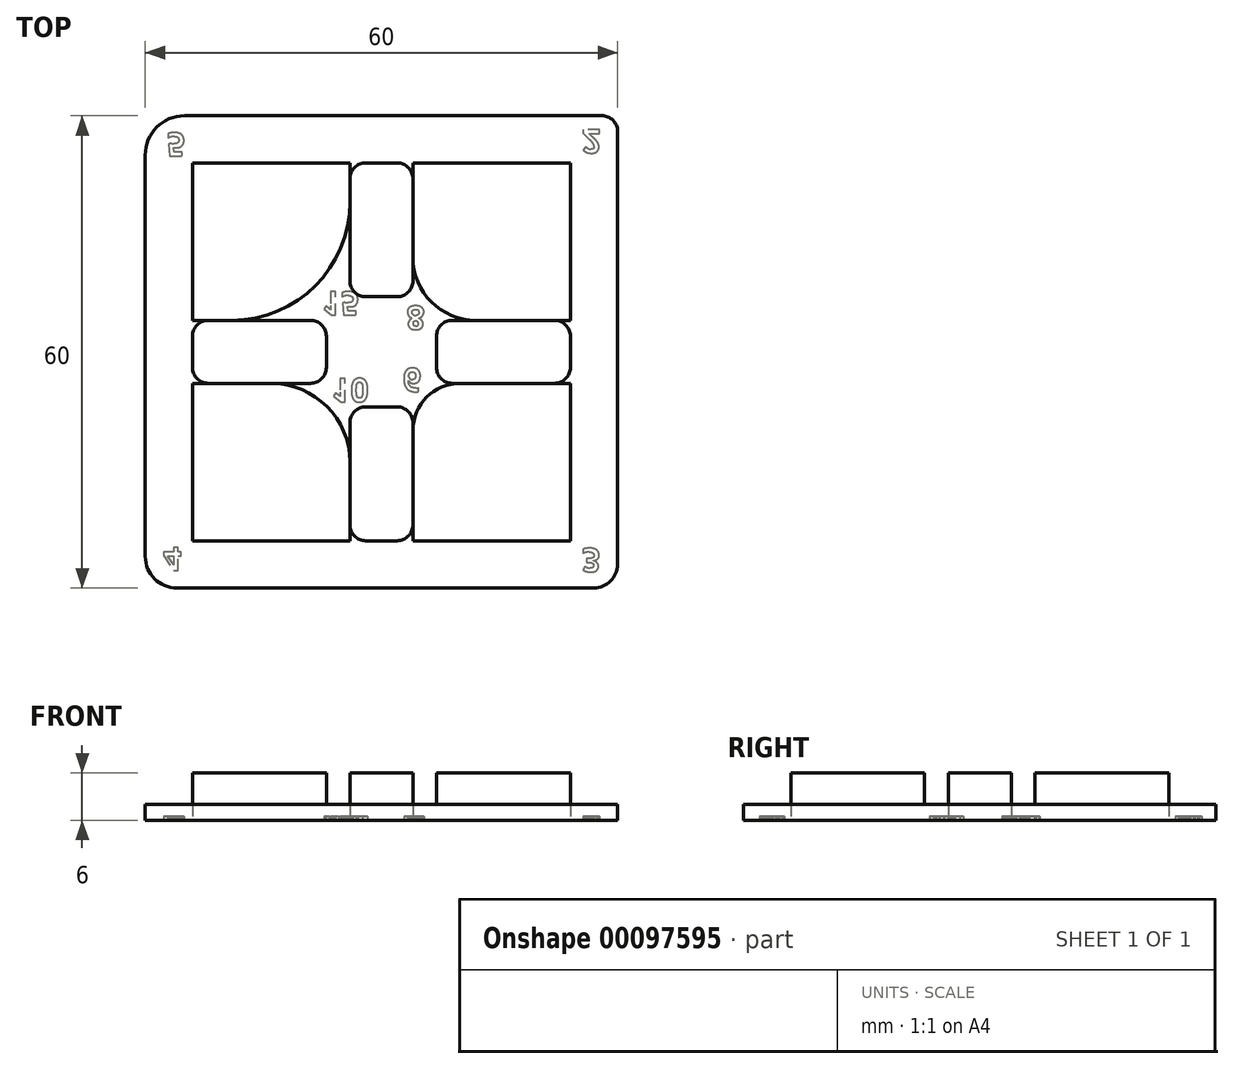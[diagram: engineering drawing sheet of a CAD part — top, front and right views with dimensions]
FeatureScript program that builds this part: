
annotation { "Feature Type Name" : "Feature", "Feature Type Description" : "" }
export const myFeature = defineFeature(function(context is Context, id is Id, definition is map)
    precondition{}
    {
        {
            var Q0;
            Q0=qCreatedBy(makeId("Top.planeOp"),FACE);
            var sketch = newSketch(context, id + "F0", { "sketchPlane" : qUnion([Q0])});
            skLineSegment(sketch, "E0.bottom", {"start": v(4, 0) * mm, "end": v(57, 0) * mm});
            skLineSegment(sketch, "E0.top", {"start": v(5, 60) * mm, "end": v(58, 60) * mm});
            skLineSegment(sketch, "E0.left", {"start": v(0, 4) * mm, "end": v(0, 55) * mm});
            skLineSegment(sketch, "E0.right", {"start": v(60, 3) * mm, "end": v(60, 58) * mm});
            skLineSegment(sketch, "E1.bottom", {"start": v(6, 6) * mm, "end": v(26, 6) * mm});
            skLineSegment(sketch, "E1.top", {"start": v(6, 26) * mm, "end": v(16, 26) * mm});
            skLineSegment(sketch, "E1.left", {"start": v(6, 6) * mm, "end": v(6, 26) * mm});
            skLineSegment(sketch, "E1.right", {"start": v(26, 6) * mm, "end": v(26, 16) * mm});
            skPoint(sketch, "E2.visualSharp", {"position": v(26, 26) * mm});
            skArc(sketch, "E2.filletArc", {"start": v(26, 16) * mm, "mid": v(23.07, 23.07) * mm, "end": v(16, 26) * mm});
            skLineSegment(sketch, "E3.bottom", {"start": v(6, 54) * mm, "end": v(26, 54) * mm});
            skLineSegment(sketch, "E3.top", {"start": v(6, 34) * mm, "end": v(11, 34) * mm});
            skLineSegment(sketch, "E3.left", {"start": v(6, 54) * mm, "end": v(6, 34) * mm});
            skLineSegment(sketch, "E3.right", {"start": v(26, 54) * mm, "end": v(26, 49) * mm});
            skPoint(sketch, "E4.visualSharp", {"position": v(26, 34) * mm});
            skArc(sketch, "E4.filletArc", {"start": v(11, 34) * mm, "mid": v(21.6, 38.4) * mm, "end": v(26, 49) * mm});
            skPoint(sketch, "E5.oppositeSnap0", {"position": v(8.5, 34) * mm});
            skLineSegment(sketch, "E5.bottom", {"start": v(54, 54) * mm, "end": v(34, 54) * mm});
            skLineSegment(sketch, "E5.top", {"start": v(54, 34) * mm, "end": v(42, 34) * mm});
            skLineSegment(sketch, "E5.left", {"start": v(54, 54) * mm, "end": v(54, 34) * mm});
            skLineSegment(sketch, "E5.right", {"start": v(34, 54) * mm, "end": v(34, 42) * mm});
            skPoint(sketch, "E6.visualSharp", {"position": v(34, 34) * mm});
            skArc(sketch, "E6.filletArc", {"start": v(34, 42) * mm, "mid": v(36.34, 36.34) * mm, "end": v(42, 34) * mm});
            skLineSegment(sketch, "E7.bottom", {"start": v(54, 6) * mm, "end": v(34, 6) * mm});
            skLineSegment(sketch, "E7.top", {"start": v(54, 26) * mm, "end": v(40, 26) * mm});
            skLineSegment(sketch, "E7.left", {"start": v(54, 6) * mm, "end": v(54, 26) * mm});
            skLineSegment(sketch, "E7.right", {"start": v(34, 6) * mm, "end": v(34, 20) * mm});
            skPoint(sketch, "E8.visualSharp", {"position": v(34, 26) * mm});
            skArc(sketch, "E8.filletArc", {"start": v(40, 26) * mm, "mid": v(35.76, 24.24) * mm, "end": v(34, 20) * mm});
            skPoint(sketch, "E9.visualSharp", {"position": v(0, 60) * mm});
            skArc(sketch, "E9.filletArc", {"start": v(5, 60) * mm, "mid": v(1.46, 58.54) * mm, "end": v(0, 55) * mm});
            skPoint(sketch, "E10.visualSharp", {"position": v(0, 0) * mm});
            skArc(sketch, "E10.filletArc", {"start": v(0, 4) * mm, "mid": v(1.17, 1.17) * mm, "end": v(4, 0) * mm});
            skPoint(sketch, "E11.visualSharp", {"position": v(60, 0) * mm});
            skArc(sketch, "E11.filletArc", {"start": v(57, 0) * mm, "mid": v(59.12, 0.88) * mm, "end": v(60, 3) * mm});
            skPoint(sketch, "E12.visualSharp", {"position": v(60, 60) * mm});
            skArc(sketch, "E12.filletArc", {"start": v(60, 58) * mm, "mid": v(59.41, 59.41) * mm, "end": v(58, 60) * mm});
            skSolve(sketch);
        }
        {
            var Q0;
            Q0=makeQuery(id+"F0.imprint","IMPRINT",FACE,{"disambiguationData":[TD([[makeQuery(id+"F0.imprint","IMPRINT",EDGE,{"derivedFrom":sQuery(id+"F0.wireOp",EDGE,"E0.bottom")}),1.0]])]});
            extrude(context, id + "F1", {"entities" : qUnion([Q0]), "depth" : 2 * mm, "offsetDistance" : 25 * mm});
        }
        {
            var Q0;
            Q0=makeQuery(id+"F1.opExtrude","CAP_FACE",FACE,{"disambiguationData":[OSD([sQuery(id+"F0.wireOp",EDGE,"E0.bottom"),sQuery(id+"F0.wireOp",EDGE,"E0.top"),sQuery(id+"F0.wireOp",EDGE,"E0.left"),sQuery(id+"F0.wireOp",EDGE,"E0.right"),sQuery(id+"F0.wireOp",EDGE,"E1.bottom"),sQuery(id+"F0.wireOp",EDGE,"E1.top"),sQuery(id+"F0.wireOp",EDGE,"E1.left"),sQuery(id+"F0.wireOp",EDGE,"E1.right"),sQuery(id+"F0.wireOp",EDGE,"E2.filletArc"),sQuery(id+"F0.wireOp",EDGE,"E3.bottom"),sQuery(id+"F0.wireOp",EDGE,"E3.top"),sQuery(id+"F0.wireOp",EDGE,"E3.left"),sQuery(id+"F0.wireOp",EDGE,"E3.right"),sQuery(id+"F0.wireOp",EDGE,"E4.filletArc"),sQuery(id+"F0.wireOp",EDGE,"E5.bottom"),sQuery(id+"F0.wireOp",EDGE,"E5.top"),sQuery(id+"F0.wireOp",EDGE,"E5.left"),sQuery(id+"F0.wireOp",EDGE,"E5.right"),sQuery(id+"F0.wireOp",EDGE,"E6.filletArc"),sQuery(id+"F0.wireOp",EDGE,"E7.bottom"),sQuery(id+"F0.wireOp",EDGE,"E7.top"),sQuery(id+"F0.wireOp",EDGE,"E7.left"),sQuery(id+"F0.wireOp",EDGE,"E7.right"),sQuery(id+"F0.wireOp",EDGE,"E8.filletArc")])],"isStart":false});
            var sketch = newSketch(context, id + "F2", { "sketchPlane" : qUnion([Q0])});
            skLineSegment(sketch, "E13.bottom", {"start": v(8, 26) * mm, "end": v(21, 26) * mm});
            skLineSegment(sketch, "E13.top", {"start": v(8, 34) * mm, "end": v(21, 34) * mm});
            skLineSegment(sketch, "E13.left", {"start": v(6, 28) * mm, "end": v(6, 32) * mm});
            skLineSegment(sketch, "E13.right", {"start": v(23, 28) * mm, "end": v(23, 32) * mm});
            skLineSegment(sketch, "E14.bottom", {"start": v(32, 54) * mm, "end": v(28, 54) * mm});
            skLineSegment(sketch, "E14.top", {"start": v(32, 37) * mm, "end": v(28, 37) * mm});
            skLineSegment(sketch, "E14.left", {"start": v(34, 52) * mm, "end": v(34, 39) * mm});
            skLineSegment(sketch, "E14.right", {"start": v(26, 52) * mm, "end": v(26, 39) * mm});
            skPoint(sketch, "E15.oppositeSnap0", {"position": v(36.34, 36.34) * mm});
            skLineSegment(sketch, "E16.bottom", {"start": v(32, 6) * mm, "end": v(28, 6) * mm});
            skLineSegment(sketch, "E16.top", {"start": v(32, 23) * mm, "end": v(28, 23) * mm});
            skLineSegment(sketch, "E16.left", {"start": v(34, 8) * mm, "end": v(34, 21) * mm});
            skLineSegment(sketch, "E16.right", {"start": v(26, 8) * mm, "end": v(26, 21) * mm});
            skLineSegment(sketch, "E17.bottom", {"start": v(52, 26) * mm, "end": v(39, 26) * mm});
            skLineSegment(sketch, "E17.top", {"start": v(52, 34) * mm, "end": v(39, 34) * mm});
            skLineSegment(sketch, "E17.left", {"start": v(54, 28) * mm, "end": v(54, 32) * mm});
            skLineSegment(sketch, "E17.right", {"start": v(37, 28) * mm, "end": v(37, 32) * mm});
            skPoint(sketch, "E18.visualSharp", {"position": v(6, 34) * mm});
            skArc(sketch, "E18.filletArc", {"start": v(8, 34) * mm, "mid": v(6.59, 33.41) * mm, "end": v(6, 32) * mm});
            skPoint(sketch, "E19.visualSharp", {"position": v(6, 26) * mm});
            skArc(sketch, "E19.filletArc", {"start": v(6, 28) * mm, "mid": v(6.59, 26.59) * mm, "end": v(8, 26) * mm});
            skPoint(sketch, "E20.visualSharp", {"position": v(23, 26) * mm});
            skArc(sketch, "E20.filletArc", {"start": v(21, 26) * mm, "mid": v(22.41, 26.59) * mm, "end": v(23, 28) * mm});
            skPoint(sketch, "E21.visualSharp", {"position": v(23, 34) * mm});
            skArc(sketch, "E21.filletArc", {"start": v(23, 32) * mm, "mid": v(22.41, 33.41) * mm, "end": v(21, 34) * mm});
            skPoint(sketch, "E22.visualSharp", {"position": v(26, 37) * mm});
            skArc(sketch, "E22.filletArc", {"start": v(26, 39) * mm, "mid": v(26.59, 37.59) * mm, "end": v(28, 37) * mm});
            skPoint(sketch, "E23.visualSharp", {"position": v(34, 37) * mm});
            skArc(sketch, "E23.filletArc", {"start": v(32, 37) * mm, "mid": v(33.41, 37.59) * mm, "end": v(34, 39) * mm});
            skPoint(sketch, "E24.visualSharp", {"position": v(34, 54) * mm});
            skArc(sketch, "E24.filletArc", {"start": v(34, 52) * mm, "mid": v(33.41, 53.41) * mm, "end": v(32, 54) * mm});
            skPoint(sketch, "E25.visualSharp", {"position": v(26, 54) * mm});
            skArc(sketch, "E25.filletArc", {"start": v(28, 54) * mm, "mid": v(26.59, 53.41) * mm, "end": v(26, 52) * mm});
            skPoint(sketch, "E26.visualSharp", {"position": v(37, 34) * mm});
            skArc(sketch, "E26.filletArc", {"start": v(39, 34) * mm, "mid": v(37.59, 33.41) * mm, "end": v(37, 32) * mm});
            skPoint(sketch, "E27.visualSharp", {"position": v(37, 26) * mm});
            skArc(sketch, "E27.filletArc", {"start": v(37, 28) * mm, "mid": v(37.59, 26.59) * mm, "end": v(39, 26) * mm});
            skPoint(sketch, "E28.visualSharp", {"position": v(54, 34) * mm});
            skArc(sketch, "E28.filletArc", {"start": v(54, 32) * mm, "mid": v(53.41, 33.41) * mm, "end": v(52, 34) * mm});
            skPoint(sketch, "E29.visualSharp", {"position": v(54, 26) * mm});
            skArc(sketch, "E29.filletArc", {"start": v(52, 26) * mm, "mid": v(53.41, 26.59) * mm, "end": v(54, 28) * mm});
            skPoint(sketch, "E30.visualSharp", {"position": v(26, 23) * mm});
            skArc(sketch, "E30.filletArc", {"start": v(28, 23) * mm, "mid": v(26.59, 22.41) * mm, "end": v(26, 21) * mm});
            skPoint(sketch, "E31.visualSharp", {"position": v(34, 23) * mm});
            skArc(sketch, "E31.filletArc", {"start": v(34, 21) * mm, "mid": v(33.41, 22.41) * mm, "end": v(32, 23) * mm});
            skPoint(sketch, "E32.visualSharp", {"position": v(34, 6) * mm});
            skArc(sketch, "E32.filletArc", {"start": v(32, 6) * mm, "mid": v(33.41, 6.59) * mm, "end": v(34, 8) * mm});
            skPoint(sketch, "E33.visualSharp", {"position": v(26, 6) * mm});
            skArc(sketch, "E33.filletArc", {"start": v(26, 8) * mm, "mid": v(26.59, 6.59) * mm, "end": v(28, 6) * mm});
            skSolve(sketch);
        }
        {
            var Q0;
            Q0 = qSketchRegion(id + "F2", true);
            extrude(context, id + "F3", {"entities" : qUnion([Q0]), "operationType" : NewBodyOperationType.ADD, "depth" : 4 * mm, "offsetDistance" : 25 * mm});
        }
        {
            var Q0;
            Q0=makeQuery(id+"F1.opExtrude","CAP_FACE",FACE,{"disambiguationData":[OSD([sQuery(id+"F0.wireOp",EDGE,"E0.bottom"),sQuery(id+"F0.wireOp",EDGE,"E0.top"),sQuery(id+"F0.wireOp",EDGE,"E0.left"),sQuery(id+"F0.wireOp",EDGE,"E0.right"),sQuery(id+"F0.wireOp",EDGE,"E1.bottom"),sQuery(id+"F0.wireOp",EDGE,"E1.top"),sQuery(id+"F0.wireOp",EDGE,"E1.left"),sQuery(id+"F0.wireOp",EDGE,"E1.right"),sQuery(id+"F0.wireOp",EDGE,"E2.filletArc"),sQuery(id+"F0.wireOp",EDGE,"E3.bottom"),sQuery(id+"F0.wireOp",EDGE,"E3.top"),sQuery(id+"F0.wireOp",EDGE,"E3.left"),sQuery(id+"F0.wireOp",EDGE,"E3.right"),sQuery(id+"F0.wireOp",EDGE,"E4.filletArc"),sQuery(id+"F0.wireOp",EDGE,"E5.bottom"),sQuery(id+"F0.wireOp",EDGE,"E5.top"),sQuery(id+"F0.wireOp",EDGE,"E5.left"),sQuery(id+"F0.wireOp",EDGE,"E5.right"),sQuery(id+"F0.wireOp",EDGE,"E6.filletArc"),sQuery(id+"F0.wireOp",EDGE,"E7.bottom"),sQuery(id+"F0.wireOp",EDGE,"E7.top"),sQuery(id+"F0.wireOp",EDGE,"E7.left"),sQuery(id+"F0.wireOp",EDGE,"E7.right"),sQuery(id+"F0.wireOp",EDGE,"E8.filletArc"),sQuery(id+"F0.wireOp",EDGE,"E9.filletArc"),sQuery(id+"F0.wireOp",EDGE,"E10.filletArc"),sQuery(id+"F0.wireOp",EDGE,"E11.filletArc"),sQuery(id+"F0.wireOp",EDGE,"E12.filletArc")])],"isStart":true});
            var sketch = newSketch(context, id + "F4", { "sketchPlane" : qUnion([Q0])});
            skText(sketch, "E34", { "text": "6\n", "fontName": "OpenSans-Bold.ttf"});
            skText(sketch, "E35", { "text": "10", "fontName": "OpenSans-Bold.ttf"});
            skText(sketch, "E36", { "text": "15", "fontName": "OpenSans-Bold.ttf"});
            skText(sketch, "E37", { "text": "8", "fontName": "OpenSans-Bold.ttf"});
            skText(sketch, "E38", { "text": "4", "fontName": "OpenSans-Bold.ttf"});
            skText(sketch, "E39", { "text": "5", "fontName": "OpenSans-Bold.ttf"});
            skText(sketch, "E40", { "text": "3", "fontName": "OpenSans-Bold.ttf"});
            skText(sketch, "E41", { "text": "2", "fontName": "OpenSans-Bold.ttf"});
            const initialGuessF4  = {"E34": [0.0327, -0.02792, 1, 0, 0.003], "E35": [0.02365, -0.02662, 1, 0, 0.003], "E36": [0.02244, -0.03763, 1, 0, 0.003], "E37": [0.03316, -0.03582, 1, 0, 0.003], "E38": [0.00223, -0.00517, 1, 0, 0.003], "E39": [0.00272, -0.05783, 1, 0, 0.003], "E40": [0.05543, -0.00503, 1, 0, 0.003], "E41": [0.05547, -0.05823, 1, 0, 0.003]};
            skSetInitialGuess(sketch, initialGuessF4);
            skSolve(sketch);
        }
        {
            var Q0;
            Q0 = qSketchRegion(id + "F4", true);
            extrude(context, id + "F5", {"entities" : qUnion([Q0]), "operationType" : NewBodyOperationType.REMOVE, "oppositeDirection" : true, "depth" : 0.5 * mm, "offsetDistance" : 25 * mm});
        }
    });
